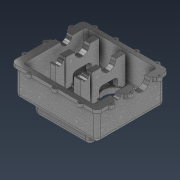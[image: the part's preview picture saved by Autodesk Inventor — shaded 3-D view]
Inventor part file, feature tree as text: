
AUTODESK INVENTOR PART (.ipt)
format: ipt  version: 2022 (Build 260153000, 153)  size: 863,744 bytes
history: native  units: mm
features: extrude x18, sketch x18, fillet x11, projected_geometry x5, hole x3, plane x3, chamfer x2
ambient origin geometry x8: Origin, YZ Plane, XZ Plane, XY Plane, X Axis, Y Axis, Z Axis, Center Point
bodies: Solid1 (feature_tree)
feature tree (60):
  extrude  "Extrusion1"  Depth=350.0mm
  extrude  "Extrusion2"  Depth=20.0mm TaperAngle=0.0deg
  extrude  "Extrusion3"  Depth=10.0mm TaperAngle=0.0deg
  extrude  "Extrusion5"  Depth=68.0mm
  extrude  "Extrusion6"  Depth=23.0mm
  extrude  "Extrusion7"  Depth=150.0mm TaperAngle=0.0deg
  extrude  "Extrusion8"  Depth=108.77mm
  sketch  "Sketch7"  dims[d33=50.0mm d34=150.0mm d35=0.0mm]
  extrude  "Extrusion9"  TaperAngle=0.0deg  [1 undecoded]
  extrude  "Extrusion10"  Depth=4.0mm TaperAngle=0.0deg
  sketch  "Sketch10"  dims[d38=90.0mm d39=0.0mm d40=0.0mm]
  hole  "Hole5"  [1 undecoded]
  extrude  "Extrusion11"  Depth=15.0mm
  extrude  "Extrusion12"  Depth=2.0mm TaperAngle=0.0deg
  extrude  "Extrusion13"  Depth=25.0mm
  extrude  "Extrusion14"  TaperAngle=0.0deg  [1 undecoded]
  extrude  "Extrusion15"  Depth=30.0mm
  fillet  "Fillet1"  Radius=40.0mm
  fillet  "Fillet2"  Radius=21.76mm
  chamfer  "Chamfer1"  Distance=10.0mm
  fillet  "Fillet3"  Radius=10.0mm
  fillet  "Fillet4"  Radius=75.0mm
  fillet  "Fillet5"  Radius=100.0mm
  fillet  "Fillet6"  Radius=250.0mm
  chamfer  "Chamfer2"  Distance=50.0mm
  plane  "Work Plane1"
  extrude  "Extrusion16"  Depth=5.0mm
  fillet  "Fillet7"  Radius=35.0mm
  fillet  "Fillet8"  Radius=35.0mm
  fillet  "Fillet9"  Radius=50.0mm
  hole  "Hole6"  [1 undecoded]
  plane  "Work Plane2"
  extrude  "Extrusion17"  Depth=5.0mm TaperAngle=45.0deg
  fillet  "Fillet11"  Radius=10.0mm
  plane  "Work Plane3"
  extrude  "Extrusion19"  Depth=5.0mm
  extrude  "Extrusion20"  Depth=20.0mm
  fillet  "Fillet12"  Radius=5.0mm
  hole  "Hole7"  [1 undecoded]
  sketch  "Sketch2"  dims[d0=290.0mm d1=350.0mm]
  sketch  "Sketch3"  dims[d19=10.0mm d20=20.0mm d21=0.0mm]
  sketch  "Sketch4"  dims[d22=100.0mm d23=0.0mm d24=10.0mm d25=0.0mm]
  sketch  "Sketch5"  dims[d28=23.172mm d29=68.0mm]
  sketch  "Sketch6"  dims[d30=150.0mm d31=0.0mm d32=23.0mm]
  sketch  "Sketch8"  dims[d36=118.76mm d37=108.77mm]
  sketch  "Sketch11"  dims[d41=105.0mm d42=4.0mm d43=20.0mm d44=0.0mm d45=0.0mm]
  sketch  "Sketch12"  dims[d46=121.5mm d47=121.5mm]
  projected_geometry  "Projected Loop1"
  sketch  "Sketch13"  dims[d48=85.5mm d49=15.0mm]
  sketch  "Sketch14"  dims[d50=20.0mm d51=0.0mm d59=2.0mm d60=0.0mm]
  sketch  "Sketch15"  dims[d82=9.376202mm d83=17.0mm d84=4.0mm d85=2.0mm d86=90.0deg d87=17.0mm d88=20.594885mm d89=25.0mm]
  sketch  "Sketch16"  dims[d90=70.0mm d91=0.0mm d92=0.0mm]
  projected_geometry  "Projected Loop2"
  projected_geometry  "Projected Loop3"
  projected_geometry  "Projected Loop4"
  sketch  "Sketch17"  dims[d93=132.118mm d94=30.0mm d95=40.0mm d96=21.76mm]
  sketch  "Sketch18"  dims[d97=228.068mm d98=10.0mm d99=0.0mm d100=10.0mm d101=0.0mm d105=75.0mm d106=100.0mm d107=250.0mm d108=50.0mm d109=-0.872665mm]
  sketch  "Sketch20"  dims[d110=5.0mm d111=5.0mm d112=35.0mm d113=35.0mm d114=50.0mm d115=-0.872665mm]
  projected_geometry  "Projected Loop5"
  sketch  "Sketch21"  dims[d116=15.0mm d117=20.0mm d118=5.0mm d119=2.0mm d120=45.0deg d121=10.0mm d122=5.0mm d123=20.0mm d124=5.0mm d125=2.0mm d126=45.0deg d127=50.0mm d128=6.0mm d129=10.0mm d130=10.0mm d131=10.0mm d132=10.0mm d134=10.0mm d135=10.0mm d136=10.0mm d137=10.0mm d138=10.0mm d140=20.0mm d143=30.0mm d144=30.0mm d145=90.0mm d146=50.0mm d147=90.0mm d148=90.0mm d149=90.0mm d150=28.75mm d151=28.75mm d153=110.0mm d154=110.0mm d155=15.0mm d156=0.0mm d157=20.0mm d158=5.0mm d159=5.0mm d160=10.0mm d161=6.647mm d162=10.0mm d163=4.0mm d164=2.0mm d165=90.0deg d166=10.0mm d167=20.594885mm d168=70.0mm d169=44.5mm d170=65.0mm d171=145.0mm d172=80.0mm d173=50.0mm d174=24.0mm d175=0.0mm d179=15.0mm d180=116.1mm d181=21.0mm d182=0.0mm d183=21.0mm d184=0.0mm d185=16.0mm d186=9.376202mm d187=17.0mm d188=4.0mm d189=2.0mm d190=90.0deg d191=17.0mm d192=20.594885mm d68=1.0mm d69=1.0mm d70=1.0mm d71=0.15mm d72=0.25mm d73=0.375mm d74=14.3117mm d75=24.0mm d76=20.594885mm d77=0.0625mm d78=0.75mm d79=0.375mm d193=0.0mm d194=0.0mm d195=0.0mm d196=0.0mm]
note: 5 required parameter values undecoded (feature->parameter linkage not recoverable at this tier; creation-order binding heuristic only, values carry confidence <= 0.55)
